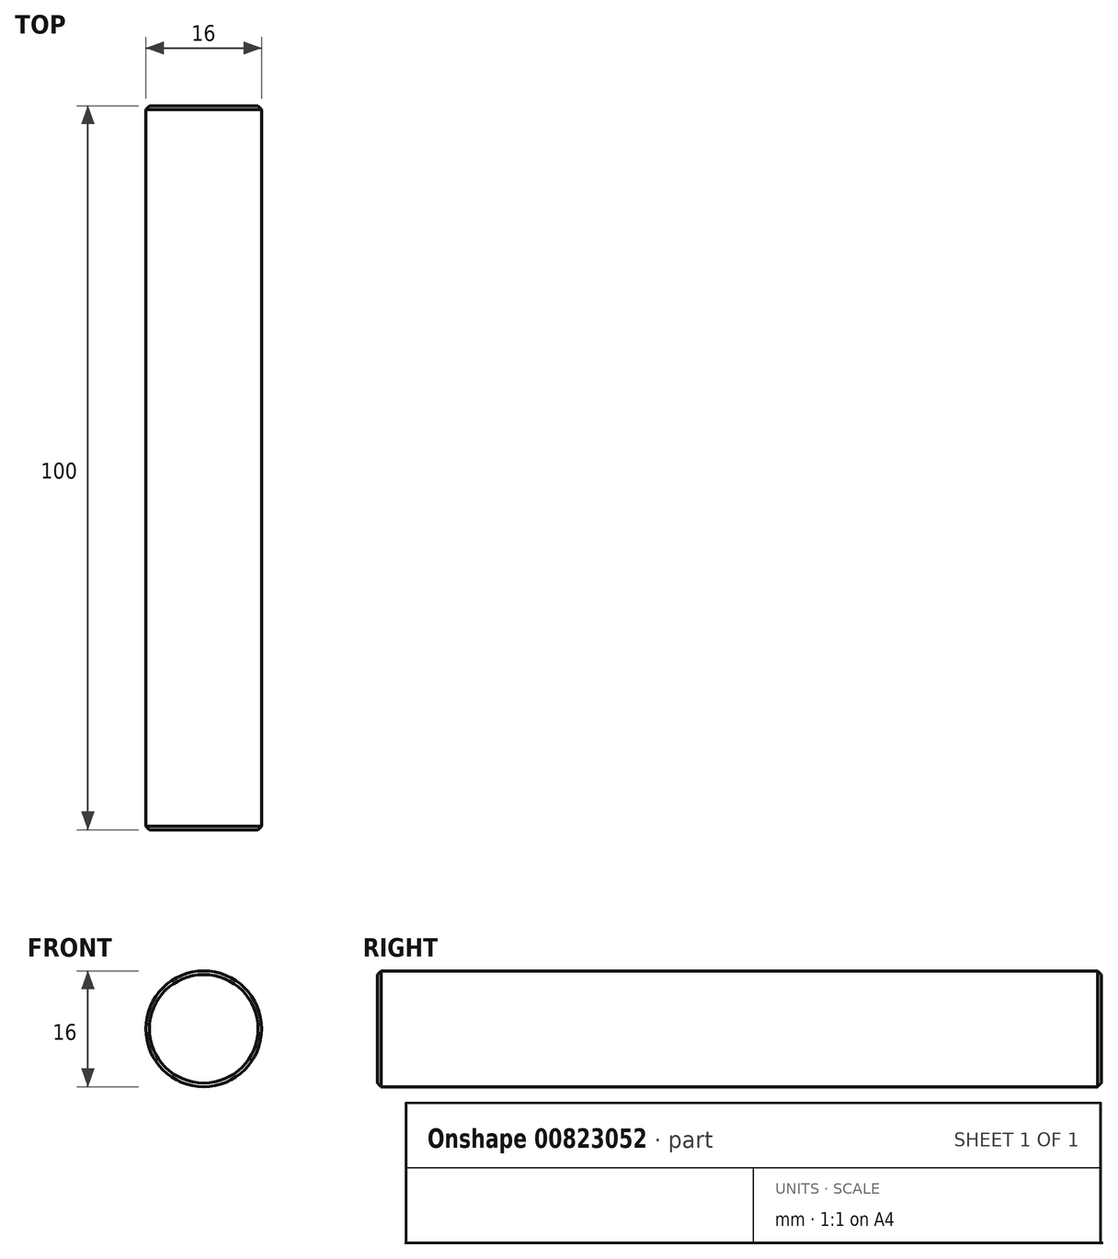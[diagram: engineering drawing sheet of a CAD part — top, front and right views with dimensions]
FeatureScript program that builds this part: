
annotation { "Feature Type Name" : "Feature", "Feature Type Description" : "" }
export const myFeature = defineFeature(function(context is Context, id is Id, definition is map)
    precondition{}
    {
        {
            var Q0;
            Q0=qCreatedBy(makeId("Front.planeOp"),FACE);
            var sketch = newSketch(context, id + "F0", { "sketchPlane" : qUnion([Q0])});
            skCircle(sketch, "E0", {"center": v(0, 0) * mm, "radius": 8 * mm});
            skSolve(sketch);
        }
        {
            var Q0;
            Q0 = qSketchRegion(id + "F0", true);
            extrude(context, id + "F1", {"entities" : qUnion([Q0]), "endBound" : BoundingType.SYMMETRIC, "depth" : 100 * mm, "offsetDistance" : 25 * mm});
        }
        {
            var Q0;
            Q0=makeQuery(id+"F1.opExtrude","SWEPT_FACE",FACE,{"disambiguationData":[OSD([sQuery(id+"F0.wireOp",EDGE,"E0")])]});
            chamfer(context, id + "F2", {"entities" : qUnion([Q0]), "width" : 0.5 * mm, "tangentPropagation" : true});
        }
    });
